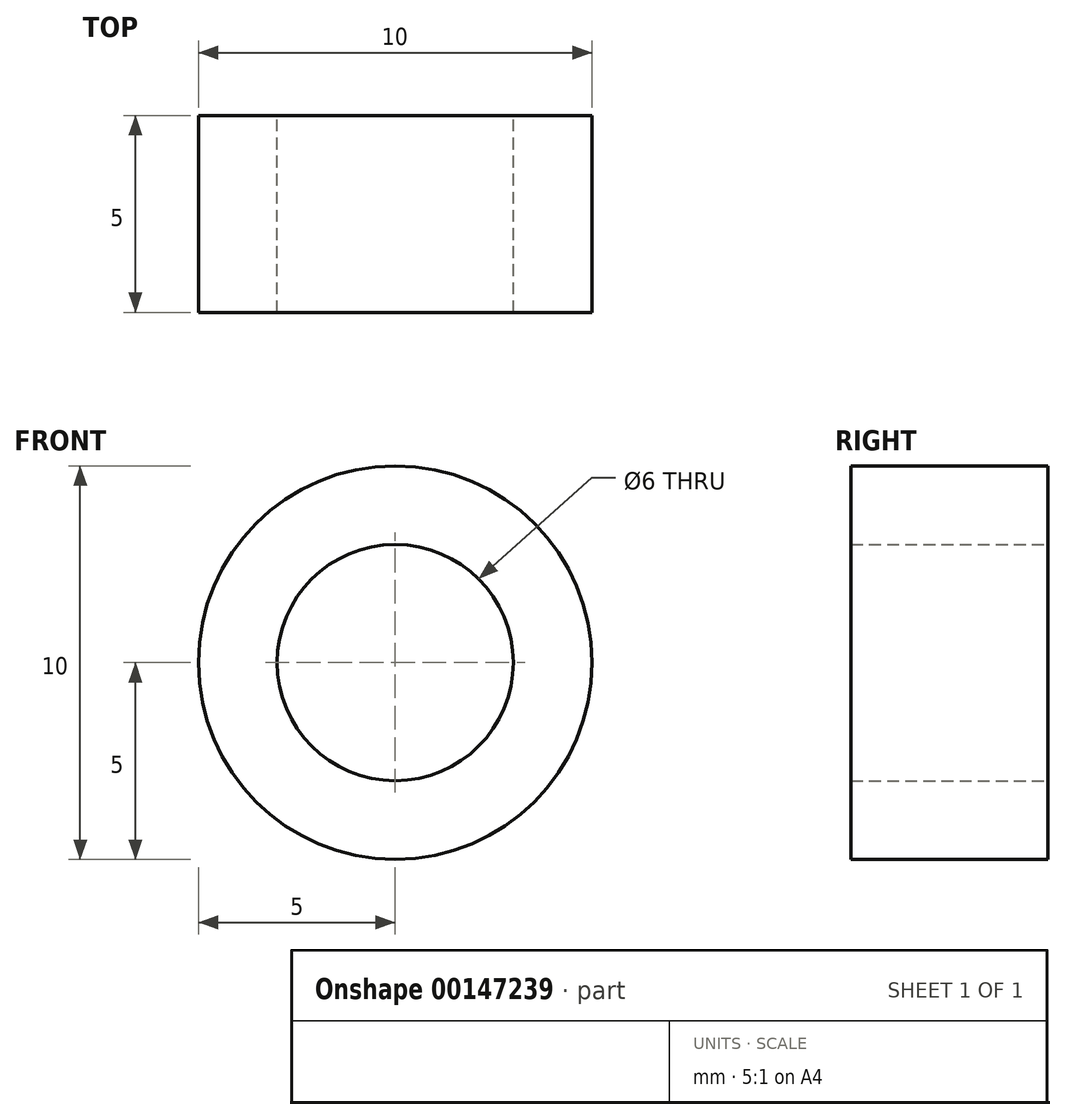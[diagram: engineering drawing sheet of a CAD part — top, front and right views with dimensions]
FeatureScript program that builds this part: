
annotation { "Feature Type Name" : "Feature", "Feature Type Description" : "" }
export const myFeature = defineFeature(function(context is Context, id is Id, definition is map)
    precondition{}
    {
        {
            var Q0;
            Q0=qCreatedBy(makeId("Front.planeOp"),FACE);
            var sketch = newSketch(context, id + "F0", { "sketchPlane" : qUnion([Q0])});
            skCircle(sketch, "E0", {"center": v(0, 0) * mm, "radius": 5 * mm});
            skCircle(sketch, "E1", {"center": v(0, 0) * mm, "radius": 3 * mm});
            skSolve(sketch);
        }
        {
            var Q0;
            Q0 = qSketchRegion(id + "F0", true);
            extrude(context, id + "F1", {"entities" : qUnion([Q0]), "depth" : 5 * mm});
        }
    });
